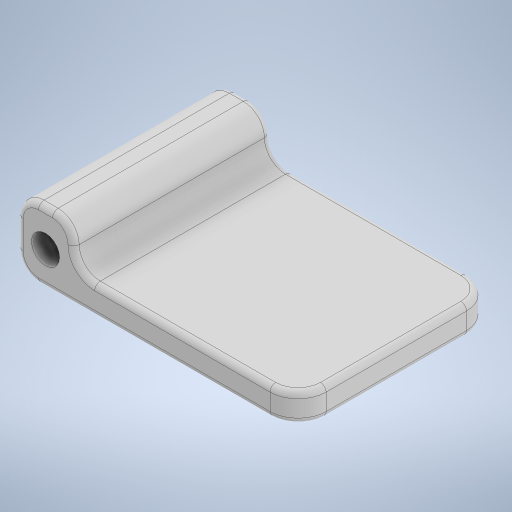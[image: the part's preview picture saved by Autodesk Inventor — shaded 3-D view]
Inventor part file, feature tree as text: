
AUTODESK INVENTOR PART (.ipt)
format: ipt  version: 2023 (Build 270158000, 158)  size: 278,528 bytes
history: native  units: in
note: dims shown in document units (in); Inventor stores cm internally (conversion verified against a paired STEP export)
features: fillet x3, extrude x1, sketch x1
ambient origin geometry x8: Origin, YZ Plane, XZ Plane, XY Plane, X Axis, Y Axis, Z Axis, Center Point
bodies: Solid1 (feature_tree)
feature tree (5):
  extrude  "Extrusion1"  Depth=1.9685in
  fillet  "Fillet1"  Radius=1.5748in
  fillet  "Fillet2"  Radius=0.7874in
  fillet  "Fillet3"  Radius=0.7874in
  sketch  "Sketch1"  dims[d0=7.874in d1=1.9685in d2=1.5748in d3=0.7874in d4=0.7874in d5=5.5118in d6=0.0in d7=0.5906in d8=0.7874in d9=0.1575in d10=0.0in]
